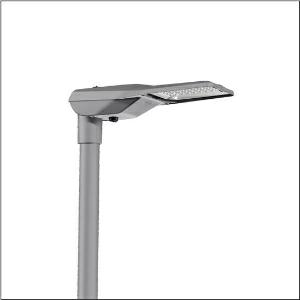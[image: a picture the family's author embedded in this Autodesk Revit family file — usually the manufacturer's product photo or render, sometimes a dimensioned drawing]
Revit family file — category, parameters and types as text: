
# Revit family: streetlight_sl_21_iq_mini___st0_8a_5xe2c31y08gb_e7ef
name_source: partatom
category: Lighting Fixtures
units: mm (PartAtom-declared; Revit-internal decimal feet)

## family parameters
Cut with Voids When Loaded = No
Host = Face
Light Source = No
Part Type = Normal
Room Calculation Point = No
Round Connector Dimension = Use Diameter
Shared = No

## types (1)
- --- (1 x LED, 5990 lm, 39.8 W, 3000K)
    Apparent Load = 40 VA
    CIE Flux Codes = 38 75 97 100 100
    Color Rendering = 70
    Color Temperature = 3000K
    Default Elevation = 1800 mm
    Description = Streetlight SL 21 iQ mini, mast luminaire, primary light control with lens, of PMMA, primary optical cover: cover, of toughened safety glass, transparent, light distribution: ST0.8a, light emission: direct distribution, primary light characteristic: asymmetric, installation type: post-top, side-entry, LED, High Power LED, rated luminous flux: 5.990lm, luminous efficacy: 151lm/W, light colour: 730, colour temperature: 3000K, control: presetting dimming logarithmic, Street-Remote, Auto-Match, Temp-Guard, Lumen-Switch, Night-Set, Smart-Wire, Light-Fading, Desk-Remote (wireless, voltage-free reading and setting of iQ features in the workshop via application-optimized NFC function/RFID function), optimised constant luminous flux control (CLO 2.0), mains connection: 220..240V, AC, 50/60Hz, start of lifetime: 40W, end of service life: 41W, reduction: 18W, luminaire housing, of diecast aluminium, powder-coated, Siteco® metallic grey (DB 702S), corrosivity category C5 mid according to DIN EN ISO 12944, please order mast flange separately, inclination adjustable: 0°, 5°, 10°, 15°, sealing non-destructively replaceable, multi-level sealing system, length: 628mm, width: 235mm, height: 110mm, mast flange for spigot size: 42mm (side-entry): 5XC10008XM4, 60/48mm (side-entry/post-top): 5XC10108XM2, 76/60mm (side-entry/post-top): 5XC10108XM1, Smart Interface below and above, protection rating (complete): IP66, insulation class (complete): insulation class II (safety insulation), certification: CE, ENEC, ENEC+, VDE, impact resistance: IK09, permissible operating ambient temperature for outdoor applications: -40..+50°C, standard-compliant lighting for roads and squares, packaging unit: 1 piece

Light Distribution: ST0.8a
    Height = 110 mm
    Lamp = 1 x LED
    Lamp Light Flux = 5990 lm
    Lamp Power = 39.8 W
    Lamp count = 1
    Length = 625 mm
    Luminous efficacy = 151 lm/W
    Manufacturer = Siteco
    ModVariant = No
    Model = 5XE2C31Y08GB
    Number of Poles = 1
    OnlyDefault = Yes
    Power Factor = 1
    Product Name = Streetlight SL 21 iQ mini | ST0.8a
    Product group = mast luminaire | pylon top
    ProductGroupID = 6100
    Protection Class = Protection class II
    Protection Degree = IP 66
    RLX_Detail_Level = 1
    RLX_Emergency_Light_Flux = 0 lm
    RLX_Emergency_Type = 0
    RLX_Emergency_Type_DB = No
    RlxData = <blob elided: 93017 chars, md5=c278cc7d>
    Socket = socket
    Standby Power = 0 W
    System Light Flux = 5990 lm
    System Power = 40 W
    Type Comments = factory setting: luminous flux: 100 % | dim-lin: 254 | 800 mA
    Type Image = l_1003514.jpg
    URL = http://relux.com
    VarID = @adj_043385
    Voltage = 0 V
    Weight = 0.00 kg
    Width = 234 mm

## geometry (parser evidence)
native form markers: Blend x4, Sweep x12
no freeform markers — native parametric forms only
